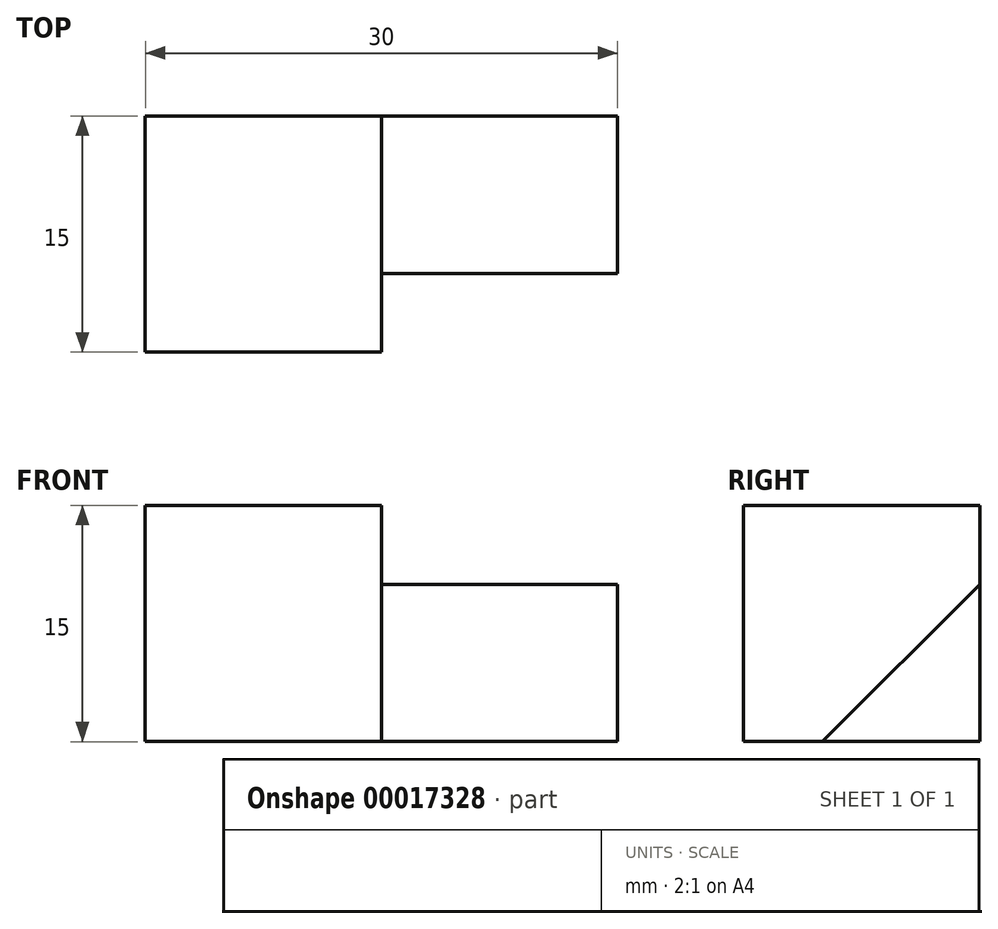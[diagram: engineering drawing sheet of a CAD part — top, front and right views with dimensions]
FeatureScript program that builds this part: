
annotation { "Feature Type Name" : "Feature", "Feature Type Description" : "" }
export const myFeature = defineFeature(function(context is Context, id is Id, definition is map)
    precondition{}
    {
        {
            var Q0;
            Q0=qCreatedBy(makeId("Front.planeOp"),FACE);
            var sketch = newSketch(context, id + "F0", { "sketchPlane" : qUnion([Q0])});
            skLineSegment(sketch, "E0.bottom", {"start": v(-1.34, 11.51) * mm, "end": v(13.66, 11.51) * mm});
            skLineSegment(sketch, "E0.top", {"start": v(-1.34, -3.49) * mm, "end": v(13.66, -3.49) * mm});
            skLineSegment(sketch, "E0.left", {"start": v(-1.34, 11.51) * mm, "end": v(-1.34, -3.49) * mm});
            skLineSegment(sketch, "E0.right", {"start": v(13.66, 11.51) * mm, "end": v(13.66, -3.49) * mm});
            skSolve(sketch);
        }
        {
            var Q0;
            Q0 = qSketchRegion(id + "F0", true);
            extrude(context, id + "F1", {"entities" : qUnion([Q0]), "oppositeDirection" : true, "depth" : 15 * mm});
        }
        {
            var Q0;
            Q0=makeQuery(id+"F1.opExtrude","SWEPT_FACE",FACE,{"disambiguationData":[OSD([sQuery(id+"F0.wireOp",EDGE,"E0.right")])]});
            var sketch = newSketch(context, id + "F2", { "sketchPlane" : qUnion([Q0])});
            skLineSegment(sketch, "E1", {"start": v(15, 6.51) * mm, "end": v(15, -3.49) * mm});
            skLineSegment(sketch, "E2", {"start": v(15, -3.49) * mm, "end": v(5, -3.49) * mm});
            skLineSegment(sketch, "E3", {"start": v(5, -3.49) * mm, "end": v(15, 6.51) * mm});
            skSolve(sketch);
        }
        {
            var Q0;
            Q0=makeQuery(id+"F2.imprint","IMPRINT",FACE,{"disambiguationData":[TD([[makeQuery(id+"F2.imprint","IMPRINT",EDGE,{"derivedFrom":sQuery(id+"F2.wireOp",EDGE,"E1")}),-1.0]])]});
            extrude(context, id + "F3", {"entities" : qUnion([Q0]), "operationType" : NewBodyOperationType.ADD, "depth" : 15 * mm});
        }
    });
